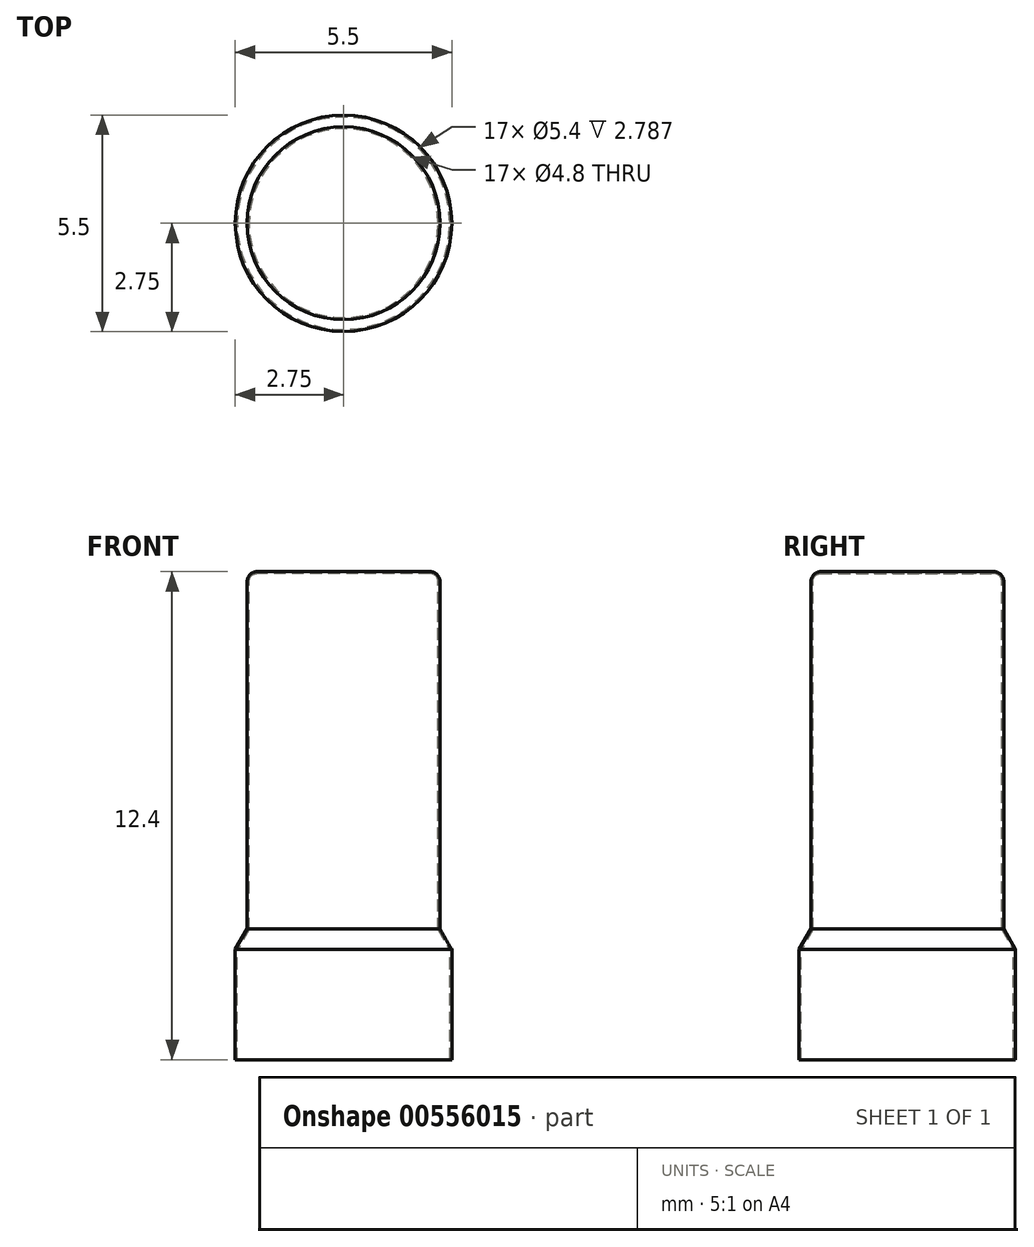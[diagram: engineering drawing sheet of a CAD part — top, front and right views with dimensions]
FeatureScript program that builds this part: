
annotation { "Feature Type Name" : "Feature", "Feature Type Description" : "" }
export const myFeature = defineFeature(function(context is Context, id is Id, definition is map)
    precondition{}
    {
        {
            var Q0;
            Q0=qCreatedBy(makeId("Front.planeOp"),FACE);
            var sketch = newSketch(context, id + "F0", { "sketchPlane" : qUnion([Q0])});
            skLineSegment(sketch, "E0", {"start": v(0, 0) * mm, "end": v(-2.2, 0) * mm});
            skLineSegment(sketch, "E1", {"start": v(-2.45, -0.25) * mm, "end": v(-2.45, -9.08) * mm});
            skLineSegment(sketch, "E2", {"start": v(-2.75, -9.6) * mm, "end": v(-2.75, -12.4) * mm});
            skLineSegment(sketch, "E3", {"start": v(-2.75, -9.6) * mm, "end": v(-2.45, -9.08) * mm});
            skPoint(sketch, "E4.visualSharp", {"position": v(-2.45, 0) * mm});
            skArc(sketch, "E4.filletArc", {"start": v(-2.2, 0) * mm, "mid": v(-2.38, -0.07) * mm, "end": v(-2.45, -0.25) * mm});
            skLineSegment(sketch, "E5.0", {"start": v(-2.7, -9.61) * mm, "end": v(-2.7, -12.4) * mm});
            skLineSegment(sketch, "E5.1", {"start": v(-2.7, -9.61) * mm, "end": v(-2.4, -9.1) * mm});
            skLineSegment(sketch, "E5.2", {"start": v(-2.4, -0.24) * mm, "end": v(-2.4, -9.1) * mm});
            skLineSegment(sketch, "E5.3", {"start": v(0, -0.05) * mm, "end": v(-2.21, -0.05) * mm});
            skPoint(sketch, "E6.visualSharp", {"position": v(-2.4, -0.05) * mm});
            skArc(sketch, "E6.filletArc", {"start": v(-2.21, -0.05) * mm, "mid": v(-2.34, -0.1) * mm, "end": v(-2.4, -0.24) * mm});
            skLineSegment(sketch, "E7", {"start": v(0, 0) * mm, "end": v(0, -0.05) * mm});
            skLineSegment(sketch, "E8", {"start": v(-2.75, -12.4) * mm, "end": v(-2.7, -12.4) * mm});
            skLineSegment(sketch, "E9", {"start": v(0, -0.05) * mm, "end": v(0, -13.02) * mm, "construction": true});
            skSolve(sketch);
        }
        {
            var Q0;
            Q0 = qSketchRegion(id + "F0", true);
            var Q1;
            Q1=sQuery(id+"F0.wireOp",EDGE,"E9");
            revolve(context, id + "F1", {"entities" : qUnion([Q0]), "axis" : qUnion([Q1]), "revolveType" : RevolveType.FULL});
        }
    });
